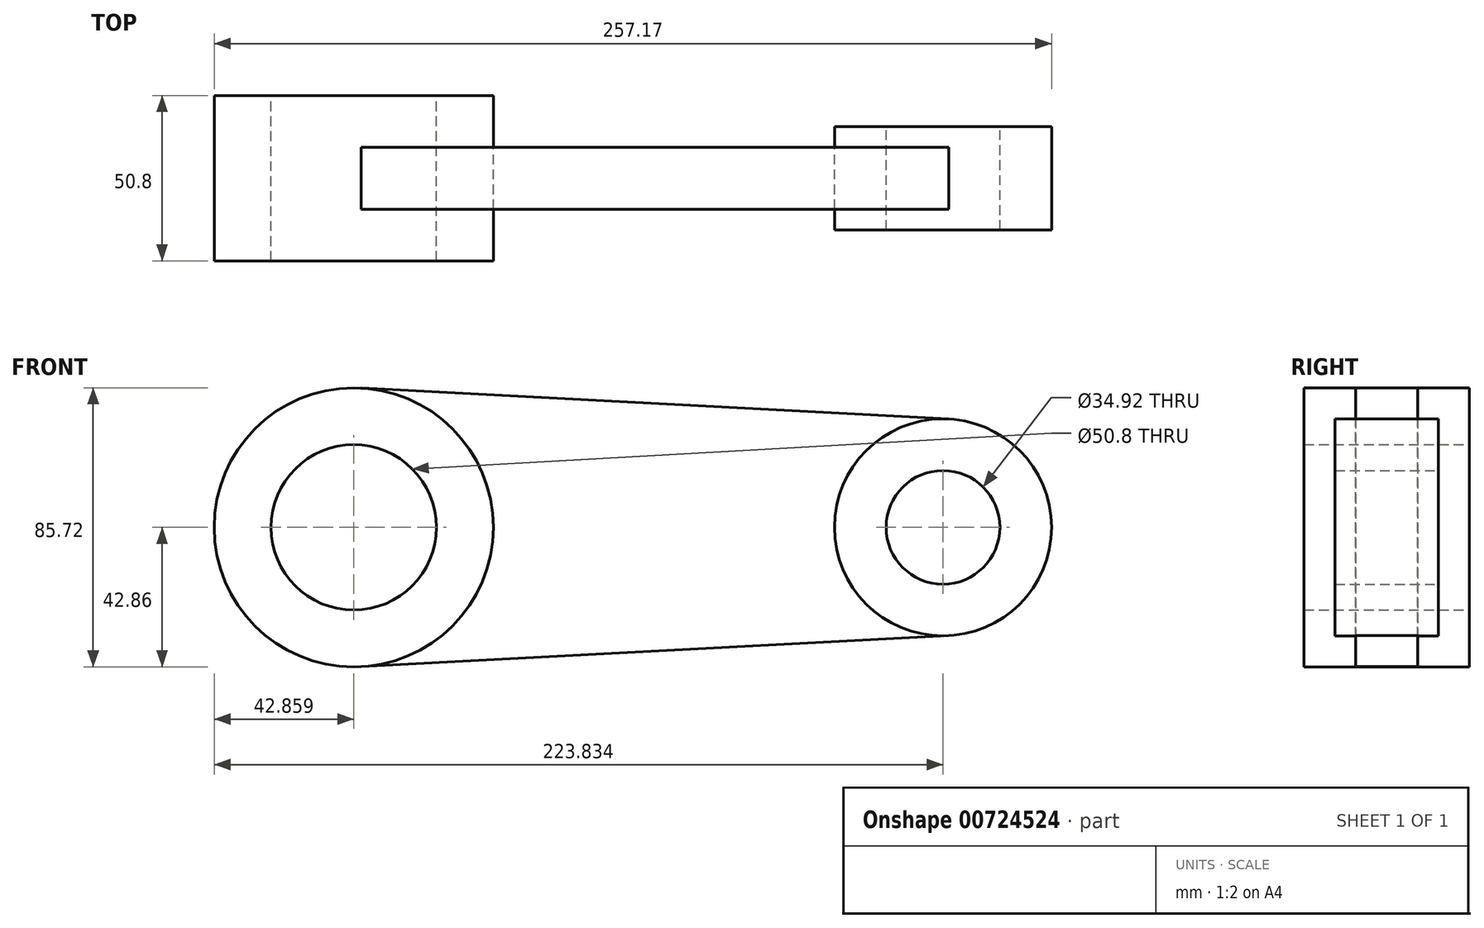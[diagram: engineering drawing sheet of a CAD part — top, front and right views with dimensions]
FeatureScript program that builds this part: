
annotation { "Feature Type Name" : "Feature", "Feature Type Description" : "" }
export const myFeature = defineFeature(function(context is Context, id is Id, definition is map)
    precondition{}
    {
        {
            var Q0;
            Q0=qCreatedBy(makeId("Front.planeOp"),FACE);
            var sketch = newSketch(context, id + "F0", { "sketchPlane" : qUnion([Q0])});
            skCircle(sketch, "E0", {"center": v(-135.67, 0) * mm, "radius": 25.4 * mm});
            skCircle(sketch, "E1", {"center": v(-135.67, 0) * mm, "radius": 42.86 * mm});
            skCircle(sketch, "E2", {"center": v(45.3, 0) * mm, "radius": 17.46 * mm});
            skCircle(sketch, "E3", {"center": v(45.3, 0) * mm, "radius": 33.34 * mm});
            skLineSegment(sketch, "E4", {"start": v(-133.42, -42.8) * mm, "end": v(47.06, -33.3) * mm});
            skLineSegment(sketch, "E5", {"start": v(-133.42, 42.8) * mm, "end": v(47.06, 33.3) * mm});
            skSolve(sketch);
        }
        {
            var Q0;
            {var subQ0=sQuery(id+"F0.wireOp",EDGE,"RluNvbC4-Xolj-I1dp-g8KM-tY4VAqvq9iQ1");var subQ1=sQuery(id+"F0.wireOp",EDGE,"E1");var subQ2=makeQuery(id+"F0.imprint","INTERSECT",VERTEX,{"disambiguationData":[OD(0.0)],"derivedFrom":[subQ1,subQ0]});Q0=makeQuery(id+"F0.imprint","IMPRINT",FACE,{"disambiguationData":[TD([[makeQuery(id+"F0.imprint","IMPRINT",EDGE,{"disambiguationData":[TD([[subQ2,1.0]])],"derivedFrom":subQ1}),1.0]])]});}
            var Q1;
            {var subQ0=sQuery(id+"F0.wireOp",EDGE,"NJSf5rRz-06eI-PsMK-ZbyU-XNEEseMUXoM8");var subQ1=sQuery(id+"F0.wireOp",EDGE,"E1");var subQ2=makeQuery(id+"F0.imprint","INTERSECT",VERTEX,{"disambiguationData":[OD(0.0)],"derivedFrom":[subQ1,subQ0]});Q1=makeQuery(id+"F0.imprint","IMPRINT",FACE,{"disambiguationData":[TD([[makeQuery(id+"F0.imprint","IMPRINT",EDGE,{"disambiguationData":[TD([[subQ2,-1.0]])],"derivedFrom":subQ1}),1.0]])]});}
            var Q2;
            Q2=makeQuery(id+"F0.imprint","IMPRINT",FACE,{"disambiguationData":[TD([[makeQuery(id+"F0.imprint","IMPRINT",EDGE,{"derivedFrom":sQuery(id+"F0.wireOp",EDGE,"E0")}),-1.0]])]});
            extrude(context, id + "F1", {"entities" : qUnion([Q0, Q1, Q2]), "endBound" : BoundingType.SYMMETRIC, "depth" : 50.8 * mm});
        }
        {
            var Q0;
            Q0=makeQuery(id+"F0.imprint","IMPRINT",FACE,{"disambiguationData":[TD([[makeQuery(id+"F0.imprint","IMPRINT",EDGE,{"derivedFrom":sQuery(id+"F0.wireOp",EDGE,"E2")}),-1.0]])]});
            extrude(context, id + "F2", {"entities" : qUnion([Q0]), "endBound" : BoundingType.SYMMETRIC, "depth" : 31.75 * mm});
        }
        {
            var Q0;
            {var subQ0=sQuery(id+"F0.wireOp",EDGE,"E4");var subQ1=sQuery(id+"F0.wireOp",EDGE,"E1");var subQ2=makeQuery(id+"F0.imprint","INTERSECT",VERTEX,{"derivedFrom":[subQ1,subQ0]});Q0=makeQuery(id+"F0.imprint","IMPRINT",FACE,{"disambiguationData":[TD([[makeQuery(id+"F0.imprint","IMPRINT",EDGE,{"disambiguationData":[TD([[subQ2,-1.0]])],"derivedFrom":subQ1}),-1.0]])]});}
            extrude(context, id + "F3", {"entities" : qUnion([Q0]), "endBound" : BoundingType.SYMMETRIC, "depth" : 19.05 * mm});
        }
    });
